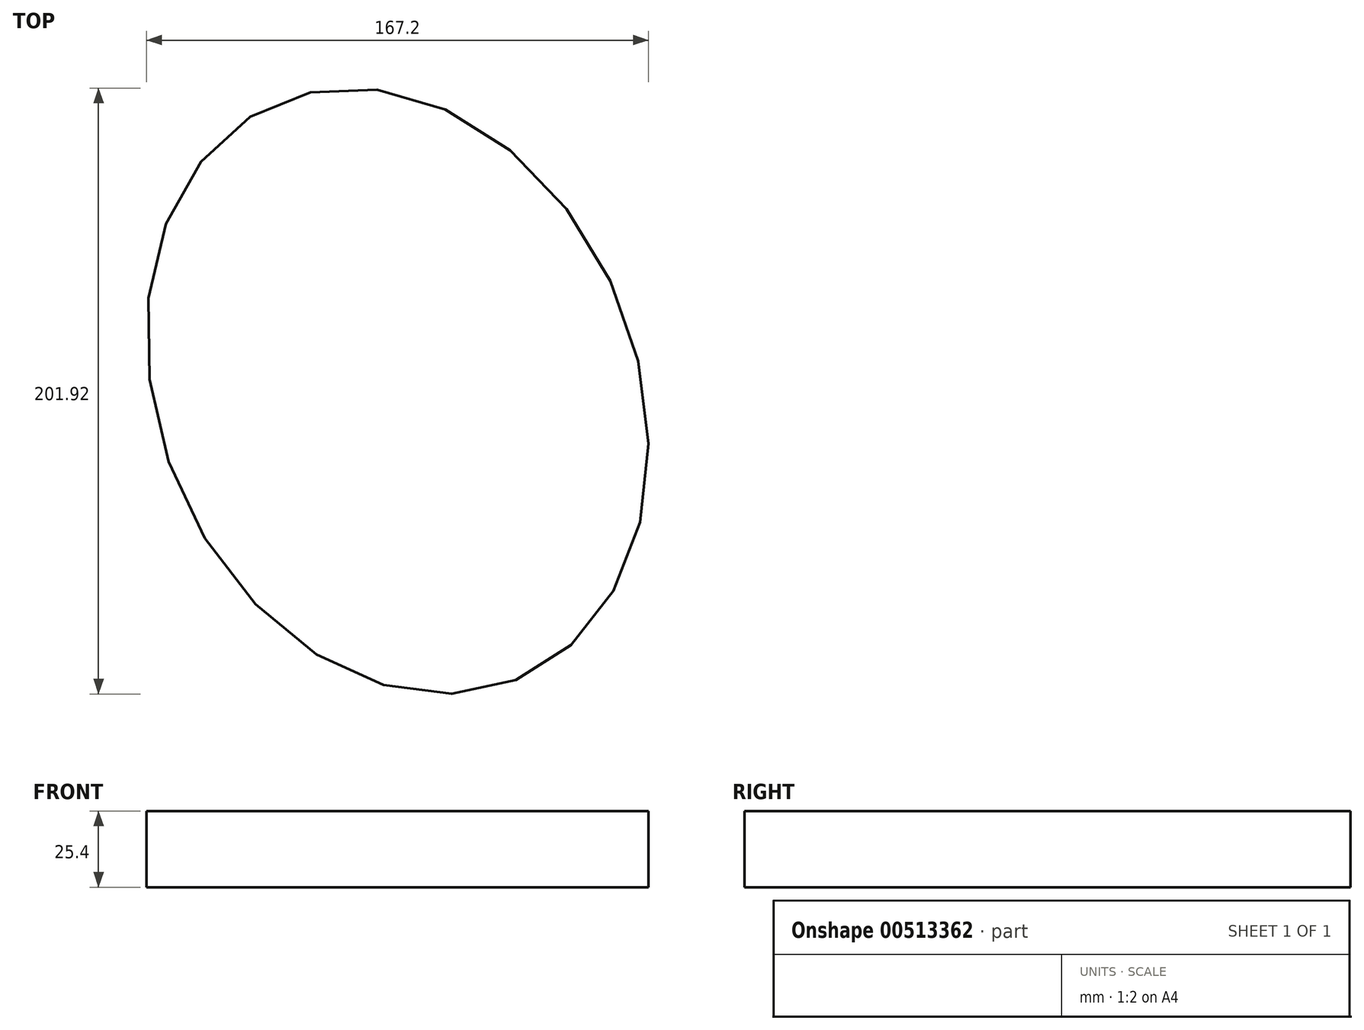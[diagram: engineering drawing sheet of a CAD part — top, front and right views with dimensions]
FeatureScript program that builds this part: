
annotation { "Feature Type Name" : "Feature", "Feature Type Description" : "" }
export const myFeature = defineFeature(function(context is Context, id is Id, definition is map)
    precondition{}
    {
        {
            var Q0;
            Q0=qCreatedBy(makeId("Top.planeOp"),FACE);
            var sketch = newSketch(context, id + "F0", { "sketchPlane" : qUnion([Q0])});
            skEllipse(sketch, "E0", {"center": v(0, 71.69) * mm, "majorRadius": 104.1 * mm, "minorRadius": 79.66 * mm, "majorAxis": v(0.38, -0.93)});
            skSolve(sketch);
        }
        {
            var Q0;
            Q0 = qSketchRegion(id + "F0", true);
            extrude(context, id + "F1", {"entities" : qUnion([Q0]), "depth" : 25.4 * mm});
        }
    });
